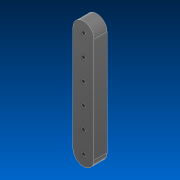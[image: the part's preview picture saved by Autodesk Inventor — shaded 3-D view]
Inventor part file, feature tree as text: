
AUTODESK INVENTOR PART (.ipt)
format: ipt  version: 2022.2 (Build 262287000, 287)  size: 97,280 bytes
history: native  units: in
note: dims shown in document units (in); Inventor stores cm internally (conversion verified against a paired STEP export)
features: sketch x1, extrude x1, hole x1
ambient origin geometry x8: Origin, YZ Plane, XZ Plane, XY Plane, X Axis, Y Axis, Z Axis, Center Point
bodies: Solid1 (feature_tree)
feature tree (3):
  sketch  "Sketch1"  dims[d0=2.5in d1=1.0in d2=1.0in d3=1.0in d4=1.0in d5=1.0in d6=0.625in d7=0.0in d8=0.17in d9=0.75in d10=0.375in d11=0.25in d12=0.5635in d13=1.0in d14=0.8108in]
  extrude  "Extrusion1"  Depth=1.0in
  hole  "Hole1"  [1 undecoded]
note: 1 required parameter value undecoded (feature->parameter linkage not recoverable at this tier; creation-order binding heuristic only, values carry confidence <= 0.55)
